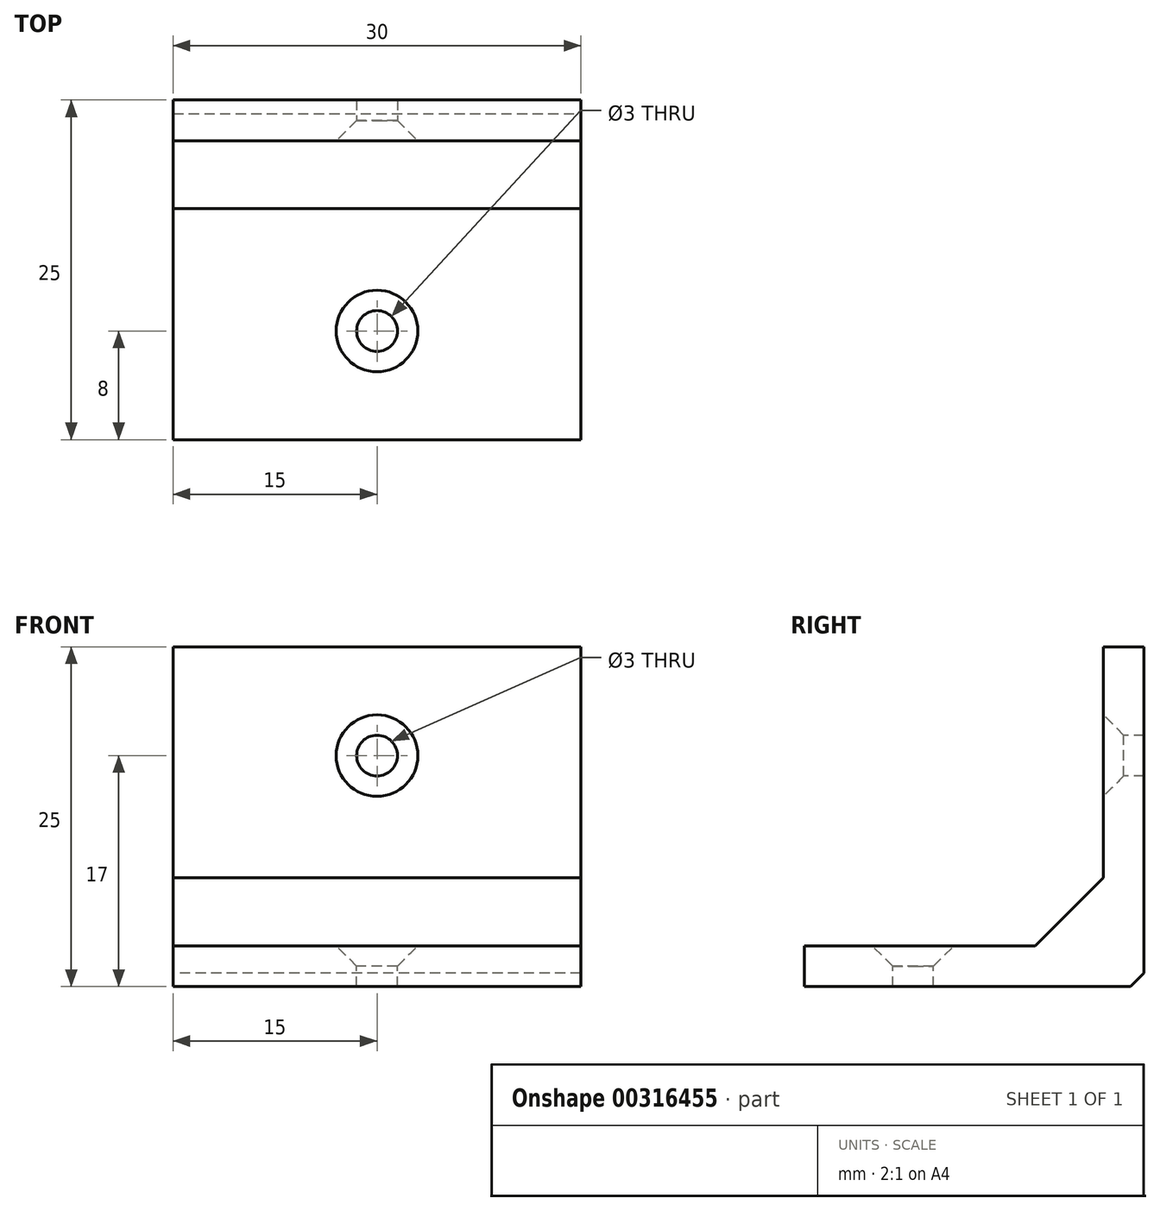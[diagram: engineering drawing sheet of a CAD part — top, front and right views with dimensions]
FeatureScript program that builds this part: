
annotation { "Feature Type Name" : "Feature", "Feature Type Description" : "" }
export const myFeature = defineFeature(function(context is Context, id is Id, definition is map)
    precondition{}
    {
        {
            var Q0;
            Q0=qCreatedBy(makeId("Right.planeOp"),FACE);
            var sketch = newSketch(context, id + "F0", { "sketchPlane" : qUnion([Q0])});
            skLineSegment(sketch, "E0", {"start": v(0, 0) * mm, "end": v(0, 25) * mm});
            skLineSegment(sketch, "E1", {"start": v(0, 25) * mm, "end": v(-3, 25) * mm});
            skLineSegment(sketch, "E2", {"start": v(-3, 25) * mm, "end": v(-3, 3) * mm});
            skLineSegment(sketch, "E3", {"start": v(-3, 3) * mm, "end": v(-25, 3) * mm});
            skLineSegment(sketch, "E4", {"start": v(-25, 3) * mm, "end": v(-25, 0) * mm});
            skLineSegment(sketch, "E5", {"start": v(-25, 0) * mm, "end": v(0, 0) * mm});
            skSolve(sketch);
        }
        {
            var Q0;
            Q0=makeQuery(id+"F0.imprint","IMPRINT",FACE,{"disambiguationData":[TD([[makeQuery(id+"F0.imprint","IMPRINT",EDGE,{"derivedFrom":sQuery(id+"F0.wireOp",EDGE,"E0")}),1.0]])]});
            extrude(context, id + "F1", {"entities" : qUnion([Q0]), "depth" : 30 * mm});
        }
        {
            var Q0;
            Q0=makeQuery(id+"F1.opExtrude","SWEPT_EDGE",EDGE,{"disambiguationData":[OSD([sQuery(id+"F0.wireOp",EDGE,"E2"),sQuery(id+"F0.wireOp",EDGE,"E3")])]});
            chamfer(context, id + "F2", {"entities" : qUnion([Q0]), "width" : 5 * mm, "tangentPropagation" : true});
        }
        {
            var Q0;
            Q0=makeQuery(id+"F1.opExtrude","SWEPT_EDGE",EDGE,{"disambiguationData":[OSD([sQuery(id+"F0.wireOp",EDGE,"E0"),sQuery(id+"F0.wireOp",EDGE,"E5")])]});
            chamfer(context, id + "F3", {"entities" : qUnion([Q0]), "width" : 1 * mm, "tangentPropagation" : true});
        }
        {
            var Q0;
            Q0=makeQuery(id+"F1.opExtrude","SWEPT_FACE",FACE,{"disambiguationData":[OSD([sQuery(id+"F0.wireOp",EDGE,"E2")])]});
            var sketch = newSketch(context, id + "F4", { "sketchPlane" : qUnion([Q0])});
            skLineSegment(sketch, "E6", {"start": v(15, 25) * mm, "end": v(15, 17) * mm});
            skSolve(sketch);
        }
        {
            var Q0;
            Q0=sQuery(id+"F4.wireOp",VERTEX,"E6.end");
            var Q1;
            Q1=makeQuery(id+"F1.opExtrude","SWEPT_BODY",BODY,{"disambiguationData":[OSD([sQuery(id+"F0.wireOp",EDGE,"E0"),sQuery(id+"F0.wireOp",EDGE,"E1"),sQuery(id+"F0.wireOp",EDGE,"E2"),sQuery(id+"F0.wireOp",EDGE,"E3"),sQuery(id+"F0.wireOp",EDGE,"E4"),sQuery(id+"F0.wireOp",EDGE,"E5")])]});
            hole(context, id + "F5", {"style" : HoleStyle.C_SINK, "endStyle" : HoleEndStyle.THROUGH, "holeDiameter" : 3 * mm, "cSinkDiameter" : 6 * mm, "cSinkAngle" : 90 * degree, "tappedDepth" : 12 * mm, "tapClearance" : 3, "locations" : qUnion([Q0]), "scope" : qUnion([Q1])});
        }
        {
            var Q0;
            Q0=makeQuery(id+"F1.opExtrude","SWEPT_FACE",FACE,{"disambiguationData":[OSD([sQuery(id+"F0.wireOp",EDGE,"E3")])]});
            var sketch = newSketch(context, id + "F6", { "sketchPlane" : qUnion([Q0])});
            skLineSegment(sketch, "E7", {"start": v(15, -25) * mm, "end": v(15, -17) * mm});
            skSolve(sketch);
        }
        {
            var Q0;
            Q0=sQuery(id+"F6.wireOp",VERTEX,"E7.end");
            var Q1;
            Q1=makeQuery(id+"F1.opExtrude","SWEPT_BODY",BODY,{"disambiguationData":[OSD([sQuery(id+"F0.wireOp",EDGE,"E0"),sQuery(id+"F0.wireOp",EDGE,"E1"),sQuery(id+"F0.wireOp",EDGE,"E2"),sQuery(id+"F0.wireOp",EDGE,"E3"),sQuery(id+"F0.wireOp",EDGE,"E4"),sQuery(id+"F0.wireOp",EDGE,"E5")])]});
            hole(context, id + "F7", {"style" : HoleStyle.C_SINK, "endStyle" : HoleEndStyle.THROUGH, "holeDiameter" : 3 * mm, "cSinkDiameter" : 6 * mm, "cSinkAngle" : 90 * degree, "tappedDepth" : 12 * mm, "tapClearance" : 3, "locations" : qUnion([Q0]), "scope" : qUnion([Q1])});
        }
    });
